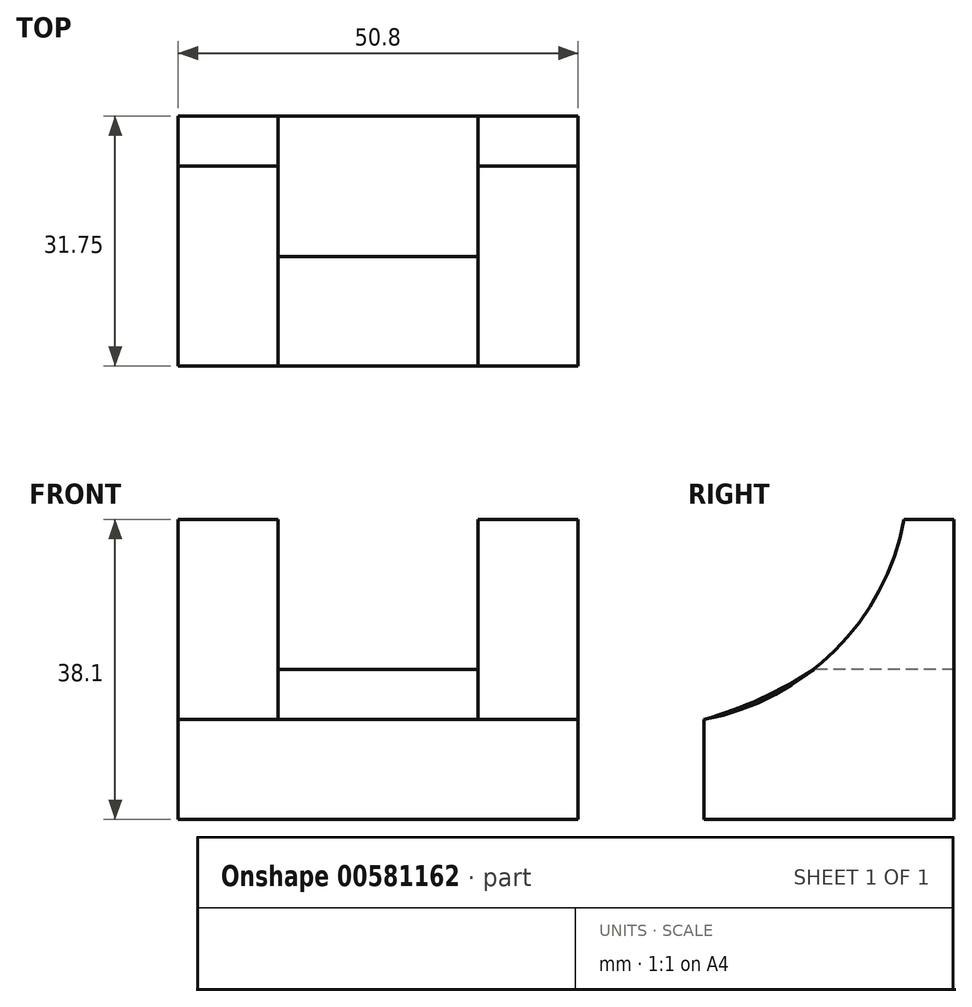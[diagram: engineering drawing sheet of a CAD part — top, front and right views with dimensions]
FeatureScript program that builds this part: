
annotation { "Feature Type Name" : "Feature", "Feature Type Description" : "" }
export const myFeature = defineFeature(function(context is Context, id is Id, definition is map)
    precondition{}
    {
        {
            var Q0;
            Q0=qCreatedBy(makeId("Front.planeOp"),FACE);
            var sketch = newSketch(context, id + "F0", { "sketchPlane" : qUnion([Q0])});
            skLineSegment(sketch, "E0", {"start": v(0, 0) * mm, "end": v(50.8, 0) * mm});
            skLineSegment(sketch, "E1", {"start": v(50.8, 0) * mm, "end": v(50.8, 38.1) * mm});
            skLineSegment(sketch, "E2", {"start": v(50.8, 38.1) * mm, "end": v(0, 38.1) * mm});
            skLineSegment(sketch, "E3", {"start": v(0, 38.1) * mm, "end": v(0, 0) * mm});
            skSolve(sketch);
        }
        {
            var Q0;
            Q0=makeQuery(id+"F0.imprint","IMPRINT",FACE,{"disambiguationData":[TD([[makeQuery(id+"F0.imprint","IMPRINT",EDGE,{"derivedFrom":sQuery(id+"F0.wireOp",EDGE,"E0")}),1.0]])]});
            extrude(context, id + "F1", {"entities" : qUnion([Q0]), "depth" : 31.75 * mm, "offsetDistance" : 25.4 * mm});
        }
        {
            var Q0;
            Q0=makeQuery(id+"F1.opExtrude","CAP_FACE",FACE,{"disambiguationData":[OSD([sQuery(id+"F0.wireOp",EDGE,"E0"),sQuery(id+"F0.wireOp",EDGE,"E1"),sQuery(id+"F0.wireOp",EDGE,"E2"),sQuery(id+"F0.wireOp",EDGE,"E3")])],"isStart":false});
            var sketch = newSketch(context, id + "F2", { "sketchPlane" : qUnion([Q0])});
            skLineSegment(sketch, "E4", {"start": v(38.1, 38.1) * mm, "end": v(38.1, 19.05) * mm});
            skLineSegment(sketch, "E5", {"start": v(38.1, 19.05) * mm, "end": v(12.7, 19.05) * mm});
            skLineSegment(sketch, "E6", {"start": v(12.7, 19.05) * mm, "end": v(12.7, 38.1) * mm});
            skLineSegment(sketch, "E7", {"start": v(12.7, 38.1) * mm, "end": v(38.1, 38.1) * mm});
            skSolve(sketch);
        }
        {
            var Q0;
            Q0=makeQuery(id+"F2.imprint","IMPRINT",FACE,{"disambiguationData":[TD([[makeQuery(id+"F2.imprint","IMPRINT",EDGE,{"derivedFrom":sQuery(id+"F2.wireOp",EDGE,"E4")}),-1.0]])]});
            extrude(context, id + "F3", {"entities" : qUnion([Q0]), "operationType" : NewBodyOperationType.REMOVE, "oppositeDirection" : true, "depth" : 31.75 * mm, "offsetDistance" : 25.4 * mm});
        }
        {
            var Q0;
            Q0=makeQuery(id+"F1.opExtrude","SWEPT_FACE",FACE,{"disambiguationData":[OSD([sQuery(id+"F0.wireOp",EDGE,"E1")])]});
            var sketch = newSketch(context, id + "F4", { "sketchPlane" : qUnion([Q0])});
            skArc(sketch, "E8", {"start": v(-31.75, 12.7) * mm, "mid": v(-15.11, 21.46) * mm, "end": v(-6.35, 38.1) * mm});
            skSolve(sketch);
        }
        {
            var Q0;
            {var subQ0=sQuery(id+"F4.wireOp",EDGE,"E8");Q0=makeQuery(id+"F4.imprint","IMPRINT",FACE,{"disambiguationData":[TD([[makeQuery(id+"F4.imprint","IMPRINT",EDGE,{"derivedFrom":subQ0}),1.0]])]});}
            extrude(context, id + "F5", {"entities" : qUnion([Q0]), "operationType" : NewBodyOperationType.REMOVE, "oppositeDirection" : true, "depth" : 12.7 * mm, "offsetDistance" : 25.4 * mm});
        }
        {
            var Q0;
            Q0=makeQuery(id+"F1.opExtrude","SWEPT_FACE",FACE,{"disambiguationData":[OSD([sQuery(id+"F0.wireOp",EDGE,"E3")])]});
            var sketch = newSketch(context, id + "F6", { "sketchPlane" : qUnion([Q0])});
            skArc(sketch, "E9", {"start": v(6.35, 38.1) * mm, "mid": v(15.11, 21.46) * mm, "end": v(31.75, 12.7) * mm});
            skSolve(sketch);
        }
        {
            var Q0;
            {var subQ0=sQuery(id+"F6.wireOp",EDGE,"E9");Q0=makeQuery(id+"F6.imprint","IMPRINT",FACE,{"disambiguationData":[TD([[makeQuery(id+"F6.imprint","IMPRINT",EDGE,{"derivedFrom":subQ0}),1.0]])]});}
            extrude(context, id + "F7", {"entities" : qUnion([Q0]), "operationType" : NewBodyOperationType.REMOVE, "oppositeDirection" : true, "depth" : 12.7 * mm, "offsetDistance" : 25.4 * mm});
        }
        {
            var Q0;
            Q0=makeQuery(id+"F5.boolean.opBoolean","COPY",FACE,{"derivedFrom":makeQuery(id+"F5.opExtrude","CAP_FACE",FACE,{"disambiguationData":[OSD([sQuery(id+"F0.wireOp",EDGE,"E1"),sQuery(id+"F0.wireOp",EDGE,"E2"),sQuery(id+"F4.wireOp",EDGE,"E8")])],"isStart":false})});
            var sketch = newSketch(context, id + "F8", { "sketchPlane" : qUnion([Q0])});
            skArc(sketch, "E10", {"start": v(-31.75, 12.7) * mm, "mid": v(-24.54, 15.35) * mm, "end": v(-17.82, 19.05) * mm});
            skSolve(sketch);
        }
        {
            var Q0;
            Q0=makeQuery(id+"F8.imprint","IMPRINT",FACE,{"disambiguationData":[TD([[makeQuery(id+"F8.imprint","IMPRINT",EDGE,{"derivedFrom":sQuery(id+"F8.wireOp",EDGE,"E10")}),1.0]])]});
            extrude(context, id + "F9", {"entities" : qUnion([Q0]), "operationType" : NewBodyOperationType.REMOVE, "oppositeDirection" : true, "depth" : 25.4 * mm, "offsetDistance" : 25.4 * mm});
        }
    });
